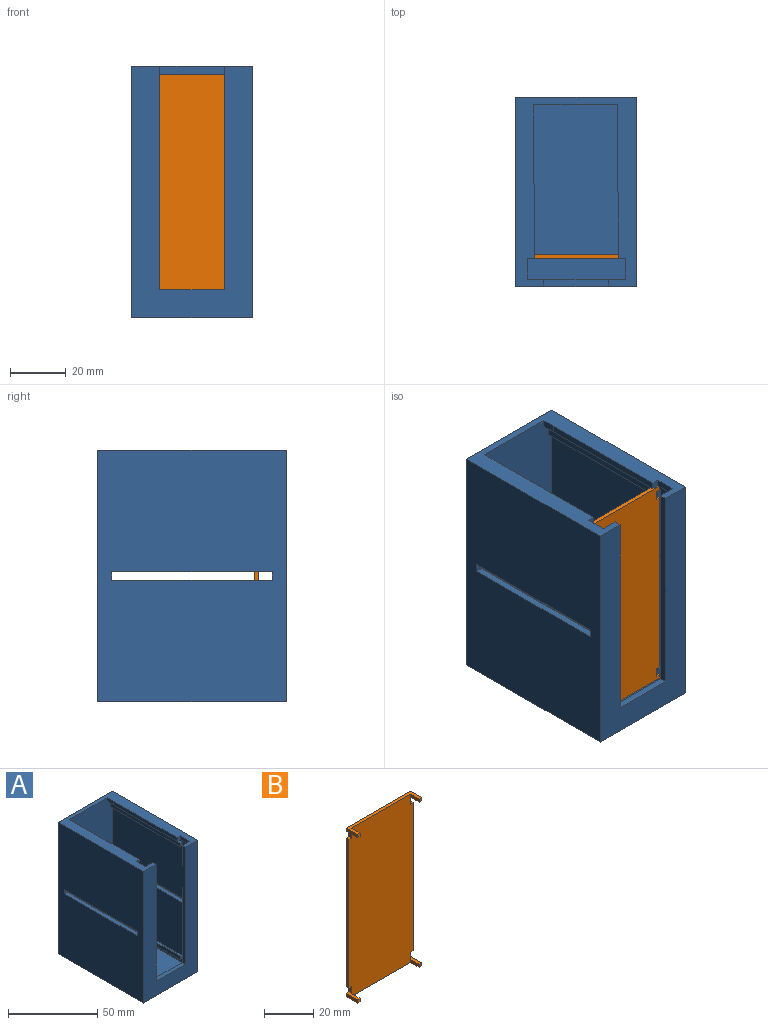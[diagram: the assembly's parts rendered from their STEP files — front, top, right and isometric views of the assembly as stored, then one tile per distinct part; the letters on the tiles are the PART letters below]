
ASSEMBLY  parts=2 mates=1
PART A: 48 faces, bbox 43x67.5x90 mm
  f0: plane 85x62.5mm, normal (1,0,0), area 4865mm2, adj f4,f6,f9,f19,f25,f26,f27,f32
  f1: plane 90x67.5mm, normal (1,0,0), area 5902.5mm2, adj f5,f7,f8,f23,f40,f41,f42,f43
  f2: plane 90x67.5mm, normal (-1,0,0), area 5902.5mm2, adj f5,f7,f8,f23,f44,f45,f46,f47
  f3: plane 85x62.5mm, normal (-1,0,0), area 4865mm2, adj f4,f9,f10,f19,f28,f30,f31,f36
  f4: plane 87.5x38mm, normal (0,-1,0), area 3290mm2, adj f0,f3,f5,f6,f9,f10,f11,f18
  f5: plane 67.5x43mm, normal (0,0,1), area 933mm2, adj f1,f2,f4,f8,f11,f12,f13,f14
  f6: plane 62.5x4.12mm, normal (0,0,-1), area 231.8mm2, adj f0,f4,f11,f12,f13,f14,f19
  f7: plane 67.5x43mm, normal (0,0,-1), area 2902.5mm2, adj f1,f2,f8,f23
  f8: plane 90x43mm, normal (0,1,0), area 3870mm2, adj f1,f2,f5,f7
  f9: plane 62.5x38mm, normal (0,0,1), area 2375mm2, adj f0,f3,f4,f19
  f10: plane 62.5x4.12mm, normal (0,0,-1), area 231.2mm2, adj f3,f4,f15,f16,f17,f18,f19
  f11: plane 5x2.5mm, normal (1,0,0), area 12.5mm2, adj f4,f5,f6,f12
  f12: plane 50x2.5mm, normal (1,0,0), area 125mm2, adj f5,f6,f11,f13
  f13: plane 2.5x2.5mm, normal (0,-1,0), area 6.2mm2, adj f5,f6,f12,f14
  f14: plane 7.5x2.5mm, normal (1,0,0), area 18.8mm2, adj f5,f6,f13,f19
  f15: plane 7.5x2.5mm, normal (-1,0,0), area 18.8mm2, adj f5,f10,f16,f19
  f16: plane 2.5x2.5mm, normal (0,-1,0), area 6.2mm2, adj f5,f10,f15,f17
  f17: plane 50x2.5mm, normal (-1,0,0), area 125mm2, adj f5,f10,f16,f18
  f18: plane 5x2.5mm, normal (-1,0,0), area 12.5mm2, adj f4,f5,f10,f17
  f19: plane 87.5x38mm, normal (0,1,0), area 1477.5mm2, adj f0,f3,f5,f6,f9,f10,f14,f15
  f20: plane 80x2.5mm, normal (-1,0,0), area 200mm2, adj f5,f19,f21,f23
  f21: plane 23x2.5mm, normal (0,0,1), area 57.5mm2, adj f19,f20,f22,f23
  f22: plane 80x2.5mm, normal (1,0,0), area 200mm2, adj f5,f19,f21,f23
  f23: plane 90x43mm, normal (0,-1,0), area 2030mm2, adj f1,f2,f5,f7,f20,f21,f22
  f24: plane 55x2.5mm, normal (1,0,0), area 137.5mm2, adj f4,f25,f26,f27
  f25: plane 55x1.5mm, normal (0,0,1), area 82.5mm2, adj f0,f4,f24,f27
  f26: plane 55x1.5mm, normal (0,0,-1), area 82.5mm2, adj f0,f4,f24,f27
  f27: plane 2.5x1.5mm, normal (0,-1,0), area 3.8mm2, adj f0,f24,f25,f26
  f28: plane 55x1.5mm, normal (0,0,1), area 82.5mm2, adj f3,f4,f29,f31
  f29: plane 55x2.5mm, normal (-1,0,0), area 137.5mm2, adj f4,f28,f30,f31
  f30: plane 55x1.5mm, normal (0,0,-1), area 82.5mm2, adj f3,f4,f29,f31
  f31: plane 2.5x1.5mm, normal (0,-1,0), area 3.7mm2, adj f3,f28,f29,f30
  f32: plane 55x1.5mm, normal (0,0,-1), area 82.5mm2, adj f0,f4,f33,f35
  f33: plane 55x2.5mm, normal (1,0,0), area 137.5mm2, adj f4,f32,f34,f35
  f34: plane 55x1.5mm, normal (0,0,1), area 82.5mm2, adj f0,f4,f33,f35
  f35: plane 2.5x1.5mm, normal (0,-1,0), area 3.7mm2, adj f0,f32,f33,f34
  f36: plane 55x1.5mm, normal (0,0,1), area 82.5mm2, adj f3,f4,f37,f39
  f37: plane 55x2.5mm, normal (-1,0,0), area 137.5mm2, adj f4,f36,f38,f39
  f38: plane 55x1.5mm, normal (0,0,-1), area 82.5mm2, adj f3,f4,f37,f39
  f39: plane 2.5x1.5mm, normal (0,-1,0), area 3.8mm2, adj f3,f36,f37,f38
  f40: plane 3x2.5mm, normal (0,-1,0), area 7.5mm2, adj f1,f3,f41,f43
  f41: plane 57.5x2.5mm, normal (0,0,-1), area 143.7mm2, adj f1,f3,f40,f42
  f42: plane 3x2.5mm, normal (0,1,0), area 7.5mm2, adj f1,f3,f41,f43
  f43: plane 57.5x2.5mm, normal (0,0,1), area 143.7mm2, adj f1,f3,f40,f42
  f44: plane 57.5x2.5mm, normal (0,0,1), area 143.7mm2, adj f0,f2,f45,f47
  f45: plane 3x2.5mm, normal (0,1,0), area 7.5mm2, adj f0,f2,f44,f46
  f46: plane 57.5x2.5mm, normal (0,0,-1), area 143.7mm2, adj f0,f2,f45,f47
  f47: plane 3x2.5mm, normal (0,-1,0), area 7.5mm2, adj f0,f2,f44,f46
PART B: 30 faces, bbox 37x6.5x84 mm
  f0: plane 84x37mm, normal (0,-1,0), area 3078mm2, adj f1,f4,f5,f6,f7,f8,f11,f14
  f1: plane 37x6.5mm, normal (0,0,-1), area 70.5mm2, adj f0,f2,f20,f21,f24,f25,f28,f29
  f2: plane 6.5x1.5mm, normal (1,0,0), area 9.8mm2, adj f1,f3,f21,f25
  f3: plane 6.5x1.5mm, normal (0,0,1), area 9.7mm2, adj f2,f4,f21,f24,f25
  f4: plane 3.5x1.5mm, normal (1,0,0), area 5.3mm2, adj f0,f3,f5,f21
  f5: plane 1.5x1.5mm, normal (0,0,-1), area 2.2mm2, adj f0,f4,f6,f21
  f6: plane 74x1.5mm, normal (1,0,0), area 111mm2, adj f0,f5,f7,f21
  f7: plane 1.5x1.5mm, normal (0,0,1), area 2.2mm2, adj f0,f6,f8,f21
  f8: plane 3.5x1.5mm, normal (1,0,0), area 5.3mm2, adj f0,f7,f9,f21
  f9: plane 6.5x1.5mm, normal (0,0,-1), area 9.7mm2, adj f8,f10,f21,f22,f23
  f10: plane 6.5x1.5mm, normal (1,0,0), area 9.8mm2, adj f9,f11,f21,f23
  f11: plane 37x6.5mm, normal (0,0,1), area 70.5mm2, adj f0,f10,f12,f21,f22,f23,f26,f27
  f12: plane 6.5x1.5mm, normal (-1,0,0), area 9.8mm2, adj f11,f13,f21,f27
  f13: plane 6.5x1.5mm, normal (0,0,-1), area 9.7mm2, adj f12,f14,f21,f26,f27
  f14: plane 3.5x1.5mm, normal (-1,0,0), area 5.3mm2, adj f0,f13,f15,f21
  f15: plane 1.5x1.5mm, normal (0,0,1), area 2.2mm2, adj f0,f14,f16,f21
  f16: plane 74x1.5mm, normal (-1,0,0), area 111mm2, adj f0,f15,f17,f21
  f17: plane 1.5x1.5mm, normal (0,0,-1), area 2.2mm2, adj f0,f16,f18,f21
  f18: plane 3.5x1.5mm, normal (-1,0,0), area 5.3mm2, adj f0,f17,f19,f21
  f19: plane 6.5x1.5mm, normal (0,0,1), area 9.7mm2, adj f18,f20,f21,f28,f29
  f20: plane 6.5x1.5mm, normal (-1,0,0), area 9.8mm2, adj f1,f19,f21,f29
  f21: plane 84x37mm, normal (0,1,0), area 3087mm2, adj f1,f2,f3,f4,f5,f6,f7,f8
  f22: plane 5x1.5mm, normal (-1,0,0), area 7.5mm2, adj f0,f9,f11,f23
  f23: plane 1.5x1.5mm, normal (0,-1,0), area 2.2mm2, adj f9,f10,f11,f22
  f24: plane 5x1.5mm, normal (-1,0,0), area 7.5mm2, adj f0,f1,f3,f25
  f25: plane 1.5x1.5mm, normal (0,-1,0), area 2.2mm2, adj f1,f2,f3,f24
  f26: plane 5x1.5mm, normal (1,0,0), area 7.5mm2, adj f0,f11,f13,f27
  f27: plane 1.5x1.5mm, normal (0,-1,0), area 2.2mm2, adj f11,f12,f13,f26
  f28: plane 5x1.5mm, normal (1,0,0), area 7.5mm2, adj f0,f1,f19,f29
  f29: plane 1.5x1.5mm, normal (0,-1,0), area 2.2mm2, adj f1,f19,f20,f28
PLACE A t=(85.1,2.5,1.4)mm fixed
PLACE B rot(axis=(1,0,0),180deg) t=(85.1,-55,1.4)mm
MATE slider B.f21 <-> A.f4  axis (0,-1,0) through (85.1,-55,1.4)mm
